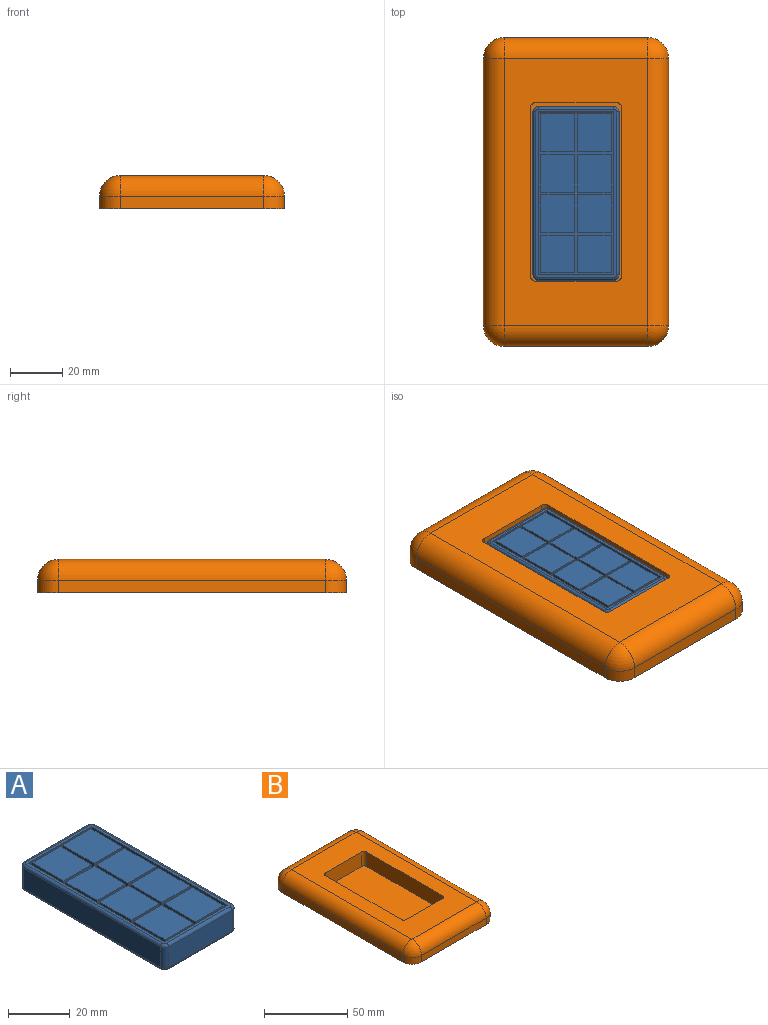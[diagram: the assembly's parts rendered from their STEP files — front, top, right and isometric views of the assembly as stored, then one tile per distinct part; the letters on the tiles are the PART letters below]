
ASSEMBLY  parts=2 mates=1
PART A: 71 faces, bbox 33.3x66.8x10.2 mm
  f0: plane 62.5x8.16mm, normal (1,0,0), area 510mm2, adj f1,f7,f62,f70
  f1: cylinder r=2mm len=8.16mm, axis (0,0,-1), area 25.6mm2, adj f0,f2,f60,f68
  f2: plane 29x8.16mm, normal (0,1,0), area 236.6mm2, adj f1,f3,f58,f66
  f3: cylinder r=2mm len=8.16mm, axis (0,0,-1), area 25.6mm2, adj f2,f4,f56,f64
  f4: plane 62.5x8.16mm, normal (-1,0,0), area 510mm2, adj f3,f5,f55,f63
  f5: cylinder r=2mm len=8.16mm, axis (0,0,-1), area 25.6mm2, adj f4,f6,f57,f65
  f6: plane 29x8.16mm, normal (0,-1,0), area 236.6mm2, adj f5,f7,f59,f67
  f7: cylinder r=2mm len=8.16mm, axis (0,0,-1), area 25.6mm2, adj f0,f6,f61,f69
  f8: plane 64.5x31mm, normal (0,0,-1), area 1998.6mm2, adj f63,f64,f65,f66,f67,f68,f69,f70
  f9: plane 29x2.54mm, normal (0,-1,0), area 73.7mm2, adj f10,f12,f13,f14
  f10: plane 62.5x2.54mm, normal (-1,0,0), area 158.8mm2, adj f9,f11,f13,f14
  f11: plane 29x2.54mm, normal (0,1,0), area 73.7mm2, adj f10,f12,f13,f14
  f12: plane 62.5x2.54mm, normal (1,0,0), area 158.8mm2, adj f9,f11,f13,f14
  f13: plane 64.5x31mm, normal (0,0,1), area 186.1mm2, adj f9,f10,f11,f12,f55,f56,f57,f58
  f14: plane 62.5x29mm, normal (0,0,1), area 304.5mm2, adj f9,f10,f11,f12,f15,f16,f17,f18
  f15: plane 13x2.54mm, normal (0,1,0), area 33mm2, adj f14,f16,f18,f19
  f16: plane 14.5x2.54mm, normal (-1,0,0), area 36.8mm2, adj f14,f15,f17,f19
  f17: plane 13x2.54mm, normal (0,-1,0), area 33mm2, adj f14,f16,f18,f19
  f18: plane 14.5x2.54mm, normal (1,0,0), area 36.8mm2, adj f14,f15,f17,f19
  f19: plane 14.5x13mm, normal (0,0,1), area 188.5mm2, adj f15,f16,f17,f18
  f20: plane 13x2.54mm, normal (0,1,0), area 33mm2, adj f14,f21,f23,f24
  f21: plane 14.5x2.54mm, normal (-1,0,0), area 36.8mm2, adj f14,f20,f22,f24
  f22: plane 13x2.54mm, normal (0,-1,0), area 33mm2, adj f14,f21,f23,f24
  f23: plane 14.5x2.54mm, normal (1,0,0), area 36.8mm2, adj f14,f20,f22,f24
  f24: plane 14.5x13mm, normal (0,0,1), area 188.5mm2, adj f20,f21,f22,f23
  f25: plane 13x2.54mm, normal (0,1,0), area 33mm2, adj f14,f26,f28,f29
  f26: plane 14.5x2.54mm, normal (-1,0,0), area 36.8mm2, adj f14,f25,f27,f29
  f27: plane 13x2.54mm, normal (0,-1,0), area 33mm2, adj f14,f26,f28,f29
  f28: plane 14.5x2.54mm, normal (1,0,0), area 36.8mm2, adj f14,f25,f27,f29
  f29: plane 14.5x13mm, normal (0,0,1), area 188.5mm2, adj f25,f26,f27,f28
  f30: plane 13x2.54mm, normal (0,1,0), area 33mm2, adj f14,f31,f33,f34
  f31: plane 14.5x2.54mm, normal (-1,0,0), area 36.8mm2, adj f14,f30,f32,f34
  f32: plane 13x2.54mm, normal (0,-1,0), area 33mm2, adj f14,f31,f33,f34
  f33: plane 14.5x2.54mm, normal (1,0,0), area 36.8mm2, adj f14,f30,f32,f34
  f34: plane 14.5x13mm, normal (0,0,1), area 188.5mm2, adj f30,f31,f32,f33
  f35: plane 13x2.54mm, normal (0,1,0), area 33mm2, adj f14,f36,f38,f39
  f36: plane 14.5x2.54mm, normal (-1,0,0), area 36.8mm2, adj f14,f35,f37,f39
  f37: plane 13x2.54mm, normal (0,-1,0), area 33mm2, adj f14,f36,f38,f39
  f38: plane 14.5x2.54mm, normal (1,0,0), area 36.8mm2, adj f14,f35,f37,f39
  f39: plane 14.5x13mm, normal (0,0,1), area 188.5mm2, adj f35,f36,f37,f38
  f40: plane 13x2.54mm, normal (0,1,0), area 33mm2, adj f14,f41,f43,f44
  f41: plane 14.5x2.54mm, normal (-1,0,0), area 36.8mm2, adj f14,f40,f42,f44
  f42: plane 13x2.54mm, normal (0,-1,0), area 33mm2, adj f14,f41,f43,f44
  f43: plane 14.5x2.54mm, normal (1,0,0), area 36.8mm2, adj f14,f40,f42,f44
  f44: plane 14.5x13mm, normal (0,0,1), area 188.5mm2, adj f40,f41,f42,f43
  f45: plane 13x2.54mm, normal (0,1,0), area 33mm2, adj f14,f46,f48,f49
  f46: plane 14.5x2.54mm, normal (-1,0,0), area 36.8mm2, adj f14,f45,f47,f49
  f47: plane 13x2.54mm, normal (0,-1,0), area 33mm2, adj f14,f46,f48,f49
  f48: plane 14.5x2.54mm, normal (1,0,0), area 36.8mm2, adj f14,f45,f47,f49
  f49: plane 14.5x13mm, normal (0,0,1), area 188.5mm2, adj f45,f46,f47,f48
  f50: plane 13x2.54mm, normal (0,1,0), area 33mm2, adj f14,f51,f53,f54
  f51: plane 14.5x2.54mm, normal (-1,0,0), area 36.8mm2, adj f14,f50,f52,f54
  f52: plane 13x2.54mm, normal (0,-1,0), area 33mm2, adj f14,f51,f53,f54
  f53: plane 14.5x2.54mm, normal (1,0,0), area 36.8mm2, adj f14,f50,f52,f54
  f54: plane 14.5x13mm, normal (0,0,1), area 188.5mm2, adj f50,f51,f52,f53
  f55: cylinder r=1mm len=62.5mm, axis (0,1,0), area 98.2mm2, adj f4,f13,f56,f57
  f56: torus R=1mm, axis (0,0,1), area 4mm2, adj f3,f13,f55,f58
  f57: torus R=1mm, axis (0,0,1), area 4mm2, adj f5,f13,f55,f59
  f58: cylinder r=1mm len=29mm, axis (1,0,0), area 45.6mm2, adj f2,f13,f56,f60
  f59: cylinder r=1mm len=29mm, axis (-1,0,0), area 45.6mm2, adj f6,f13,f57,f61
  f60: torus R=1mm, axis (0,0,1), area 4mm2, adj f1,f13,f58,f62
  f61: torus R=1mm, axis (0,0,1), area 4mm2, adj f7,f13,f59,f62
  f62: cylinder r=1mm len=62.5mm, axis (0,-1,0), area 98.2mm2, adj f0,f13,f60,f61
  f63: cylinder r=1mm len=62.5mm, axis (0,-1,0), area 98.2mm2, adj f4,f8,f64,f65
  f64: torus R=1mm, axis (0,0,1), area 4mm2, adj f3,f8,f63,f66
  f65: torus R=1mm, axis (0,0,1), area 4mm2, adj f5,f8,f63,f67
  f66: cylinder r=1mm len=29mm, axis (-1,0,0), area 45.6mm2, adj f2,f8,f64,f68
  f67: cylinder r=1mm len=29mm, axis (1,0,0), area 45.6mm2, adj f6,f8,f65,f69
  f68: torus R=1mm, axis (0,0,1), area 4mm2, adj f1,f8,f66,f70
  f69: torus R=1mm, axis (0,0,1), area 4mm2, adj f7,f8,f67,f70
  f70: cylinder r=1mm len=62.5mm, axis (0,1,0), area 98.2mm2, adj f0,f8,f68,f69
PART B: 71 faces, bbox 71x118.5x12.7 mm
  f0: plane 31x10.7mm, normal (0,1,0), area 157.7mm2, adj f6,f7,f19,f47,f60,f61,f62
  f1: plane 31x10.7mm, normal (0,-1,0), area 157.7mm2, adj f2,f37,f38,f47,f60,f61,f62
  f2: plane 72.5x39mm, normal (0,0,-1), area 2813.8mm2, adj f1,f35,f36,f37,f38,f39,f40,f41
  f3: plane 118.5x71mm, normal (0,0,-1), area 718mm2, adj f10,f11,f12,f13,f14,f15,f16,f17
  f4: cylinder r=2mm len=10.7mm, axis (0,0,-1), area 33.6mm2, adj f5,f18,f19,f60
  f5: plane 64.5x10.7mm, normal (-1,0,0), area 690.1mm2, adj f4,f6,f19,f60
  f6: cylinder r=2mm len=10.7mm, axis (0,0,-1), area 33.6mm2, adj f0,f5,f19,f60
  f7: cylinder r=2mm len=10.7mm, axis (0,0,-1), area 33.6mm2, adj f0,f8,f19,f60
  f8: plane 64.5x10.7mm, normal (1,0,0), area 690.1mm2, adj f7,f9,f19,f60
  f9: cylinder r=2mm len=10.7mm, axis (0,0,-1), area 33.6mm2, adj f8,f18,f19,f60
  f10: plane 102.5x4.7mm, normal (1,0,0), area 481.7mm2, adj f3,f11,f17,f27
  f11: cylinder r=8mm len=8mm, axis (0,0,-1), area 59.1mm2, adj f3,f10,f12,f25
  f12: plane 55x4.7mm, normal (0,1,0), area 258.5mm2, adj f3,f11,f13,f23
  f13: cylinder r=8mm len=8mm, axis (0,0,-1), area 59.1mm2, adj f3,f12,f14,f21
  f14: plane 102.5x4.7mm, normal (-1,0,0), area 481.7mm2, adj f3,f13,f15,f20
  f15: cylinder r=8mm len=8mm, axis (0,0,-1), area 59.1mm2, adj f3,f14,f16,f22
  f16: plane 55x4.7mm, normal (0,-1,0), area 258.5mm2, adj f3,f15,f17,f24
  f17: cylinder r=8mm len=8mm, axis (0,0,-1), area 59.1mm2, adj f3,f10,f16,f26
  f18: plane 31x10.7mm, normal (0,-1,0), area 331.7mm2, adj f4,f9,f19,f60
  f19: plane 102.5x55mm, normal (0,0,1), area 3243.4mm2, adj f0,f4,f5,f6,f7,f8,f9,f18
  f20: cylinder r=8mm len=102.5mm, axis (0,1,0), area 1288.1mm2, adj f14,f19,f21,f22
  f21: sphere r=8mm, area 100.5mm2, adj f13,f20,f23
  f22: sphere r=8mm, area 100.5mm2, adj f15,f20,f24
  f23: cylinder r=8mm len=55mm, axis (1,0,0), area 691.2mm2, adj f12,f19,f21,f25
  f24: cylinder r=8mm len=55mm, axis (-1,0,0), area 691.2mm2, adj f16,f19,f22,f26
  f25: sphere r=8mm, area 100.5mm2, adj f11,f23,f27
  f26: sphere r=8mm, area 100.5mm2, adj f17,f24,f27
  f27: cylinder r=8mm len=102.5mm, axis (0,-1,0), area 1288.1mm2, adj f10,f19,f25,f26
  f28: plane 102.5x4.7mm, normal (1,0,0), area 481.7mm2, adj f3,f29,f46,f49
  f29: cylinder r=6mm len=6mm, axis (0,0,-1), area 44.3mm2, adj f3,f28,f30,f51
  f30: plane 55x4.7mm, normal (0,1,0), area 258.5mm2, adj f3,f29,f31,f53
  f31: cylinder r=6mm len=6mm, axis (0,0,-1), area 44.3mm2, adj f3,f30,f32,f55
  f32: plane 102.5x4.7mm, normal (-1,0,0), area 481.7mm2, adj f3,f31,f33,f54
  f33: cylinder r=6mm len=6mm, axis (0,0,-1), area 44.3mm2, adj f3,f32,f34,f52
  f34: plane 55x4.7mm, normal (0,-1,0), area 258.5mm2, adj f3,f33,f46,f50
  f35: cylinder r=4mm len=10.7mm, axis (0,0,-1), area 67.2mm2, adj f2,f36,f41,f47
  f36: plane 64.5x10.7mm, normal (1,0,0), area 690.1mm2, adj f2,f35,f37,f47
  f37: cylinder r=4mm len=10.7mm, axis (0,0,-1), area 67.2mm2, adj f1,f2,f36,f47
  f38: cylinder r=4mm len=10.7mm, axis (0,0,-1), area 67.2mm2, adj f1,f2,f39,f47
  f39: plane 64.5x10.7mm, normal (-1,0,0), area 690.1mm2, adj f2,f38,f40,f47
  f40: cylinder r=4mm len=10.7mm, axis (0,0,-1), area 67.2mm2, adj f2,f39,f41,f47
  f41: plane 31x10.7mm, normal (0,1,0), area 331.7mm2, adj f2,f35,f40,f47
  f42: cylinder r=3mm len=10.7mm, axis (0,0,-1), area 194.2mm2, adj f47,f48,f49,f50,f59
  f43: cylinder r=3mm len=10.7mm, axis (0,0,-1), area 194.2mm2, adj f47,f49,f51,f53,f58
  f44: cylinder r=3mm len=10.7mm, axis (0,0,-1), area 194.2mm2, adj f47,f53,f54,f55,f57
  f45: cylinder r=3mm len=10.7mm, axis (0,0,-1), area 194.2mm2, adj f47,f50,f52,f54,f56
  f46: cylinder r=6mm len=6mm, axis (0,0,-1), area 44.3mm2, adj f3,f28,f34,f48
  f47: plane 102.5x55mm, normal (0,0,-1), area 2835.5mm2, adj f0,f1,f35,f36,f37,f38,f39,f40
  f48: sphere r=6mm, area 49mm2, adj f42,f46,f49,f50
  f49: cylinder r=6mm len=102.5mm, axis (0,1,0), area 951.4mm2, adj f28,f42,f43,f47,f48,f51
  f50: cylinder r=6mm len=55mm, axis (1,0,0), area 503.7mm2, adj f34,f42,f45,f47,f48,f52
  f51: sphere r=6mm, area 49mm2, adj f29,f43,f49,f53
  f52: sphere r=6mm, area 49mm2, adj f33,f45,f50,f54
  f53: cylinder r=6mm len=55mm, axis (-1,0,0), area 503.7mm2, adj f30,f43,f44,f47,f51,f55
  f54: cylinder r=6mm len=102.5mm, axis (0,-1,0), area 951.4mm2, adj f32,f44,f45,f47,f52,f55
  f55: sphere r=6mm, area 49mm2, adj f31,f44,f53,f54
  f56: plane 6x6mm, normal (0,0,-1), area 25.1mm2, adj f45,f69
  f57: plane 6x6mm, normal (0,0,-1), area 25.1mm2, adj f44,f67
  f58: plane 6x6mm, normal (0,0,-1), area 25.1mm2, adj f43,f65
  f59: plane 6x6mm, normal (0,0,-1), area 25.1mm2, adj f42,f63
  f60: plane 70.5x35mm, normal (0,0,1), area 2434.1mm2, adj f0,f1,f4,f5,f6,f7,f8,f9
  f61: plane 8.7x2mm, normal (-1,0,0), area 17.4mm2, adj f0,f1,f47,f60
  f62: plane 8.7x2mm, normal (1,0,0), area 17.4mm2, adj f0,f1,f47,f60
  f63: cylinder r=1mm len=5mm, axis (0,0,-1), area 31.4mm2, adj f59,f64
  f64: plane 2x2mm, normal (0,0,-1), area 3.1mm2, adj f63
  f65: cylinder r=1mm len=5mm, axis (0,0,-1), area 31.4mm2, adj f58,f66
  f66: plane 2x2mm, normal (0,0,-1), area 3.1mm2, adj f65
  f67: cylinder r=1mm len=5mm, axis (0,0,-1), area 31.4mm2, adj f57,f68
  f68: plane 2x2mm, normal (0,0,-1), area 3.1mm2, adj f67
  f69: cylinder r=1mm len=5mm, axis (0,0,-1), area 31.4mm2, adj f56,f70
  f70: plane 2x2mm, normal (0,0,-1), area 3.1mm2, adj f69
PLACE A t=(0.52,-1.53,-6.72)mm
PLACE B t=(0.52,-0.95,-9.22)mm fixed
MATE slider B.f60 <-> A.f8  axis (0,0,1) through (0.52,-1.53,-7.22)mm
